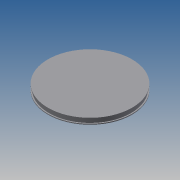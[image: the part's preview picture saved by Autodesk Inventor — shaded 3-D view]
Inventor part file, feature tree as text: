
AUTODESK INVENTOR PART (.ipt)
format: ipt  version: 2013 (Build 170138000, 138)  size: 110,592 bytes
history: native  units: mm
features: extrude x6, sketch x6
ambient origin geometry x8: Origin, YZ Plane, XZ Plane, XY Plane, X Axis, Y Axis, Z Axis, Center Point
bodies: Solid1 (feature_tree)
feature tree (12):
  extrude  "Extrusion1"  Depth=1.5mm TaperAngle=0.0deg
  extrude  "Extrusion2"  Depth=1.5mm TaperAngle=0.0deg
  extrude  "Extrusion3"  Depth=2.0mm TaperAngle=0.0deg
  extrude  "Extrusion5"  Depth=154.0mm
  extrude  "Extrusion6"  Depth=7.0mm TaperAngle=0.0deg
  extrude  "Extrusion4"  [1 undecoded]
  sketch  "Sketch1"  dims[d0=66.0mm d2=1.5mm d3=0.0mm]
  sketch  "Sketch2"  dims[d6=7.0mm d7=0.0mm d8=1.5mm d9=0.0mm]
  sketch  "Sketch3"  dims[d10=12.5mm d12=2.0mm d13=0.0mm]
  sketch  "Sketch4"  dims[d15=2.0mm d16=154.0mm]
  sketch  "Sketch5"  dims[d18=150.0mm d20=7.0mm d21=0.0mm]
  sketch  "Sketch6"  dims[d22=1.5mm d23=0.0mm]
note: 1 required parameter value undecoded (feature->parameter linkage not recoverable at this tier; creation-order binding heuristic only, values carry confidence <= 0.55)
